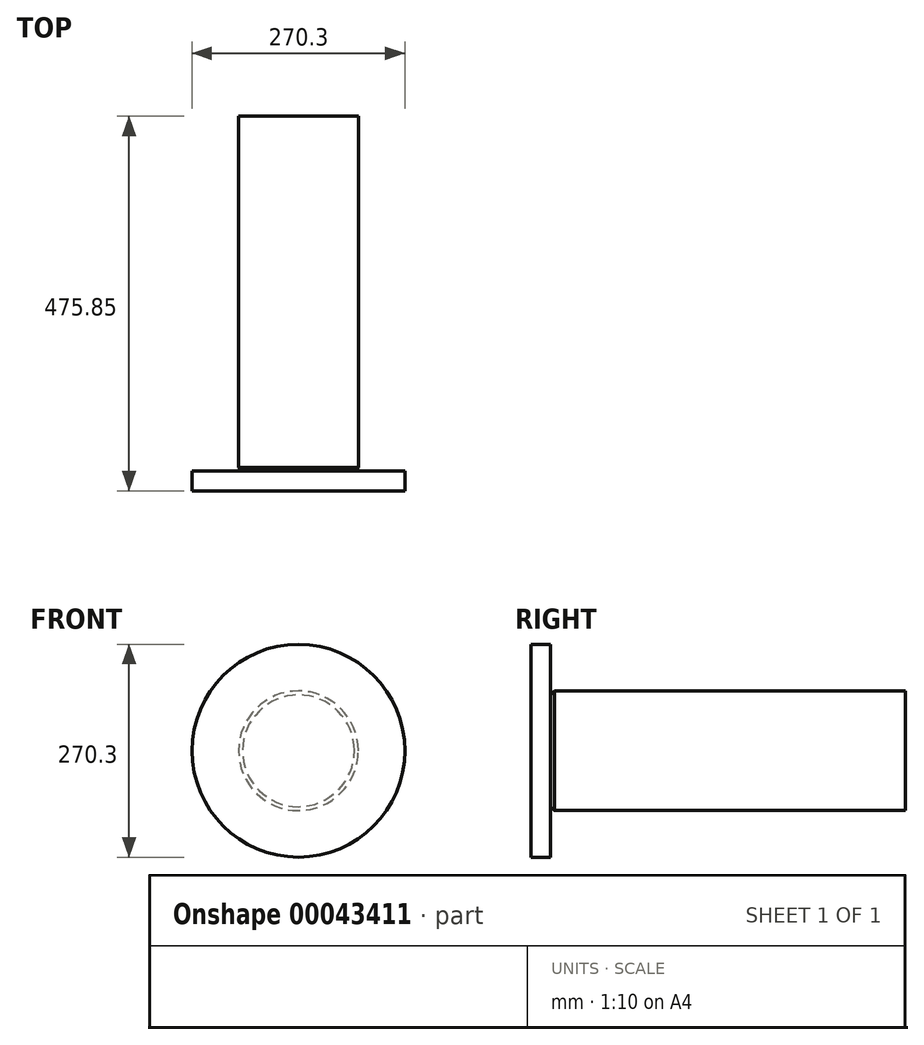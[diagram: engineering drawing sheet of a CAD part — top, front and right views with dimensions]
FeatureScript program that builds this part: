
annotation { "Feature Type Name" : "Feature", "Feature Type Description" : "" }
export const myFeature = defineFeature(function(context is Context, id is Id, definition is map)
    precondition{}
    {
        {
            var Q0;
            Q0=qCreatedBy(makeId("Front.planeOp"),FACE);
            var sketch = newSketch(context, id + "F0", { "sketchPlane" : qUnion([Q0])});
            skCircle(sketch, "E0", {"center": v(0, 0) * mm, "radius": 76 * mm});
            skSolve(sketch);
        }
        {
            var Q0;
            Q0=makeQuery(id+"F0.imprint","IMPRINT",FACE,{"disambiguationData":[TD([[makeQuery(id+"F0.imprint","IMPRINT",EDGE,{"derivedFrom":sQuery(id+"F0.wireOp",EDGE,"E0")}),1.0]])]});
            extrude(context, id + "F1", {"entities" : qUnion([Q0]), "oppositeDirection" : true, "depth" : 450.85 * mm});
        }
        {
            var Q0;
            Q0=makeQuery(id+"F1.opExtrude","CAP_EDGE",EDGE,{"disambiguationData":[OSD([sQuery(id+"F0.wireOp",EDGE,"E0")])],"isStart":true});
            chamfer(context, id + "F2", {"entities" : qUnion([Q0]), "width" : 5 * mm, "tangentPropagation" : true});
        }
        {
            var Q0;
            Q0=qCreatedBy(makeId("Front.planeOp"),FACE);
            var sketch = newSketch(context, id + "F3", { "sketchPlane" : qUnion([Q0])});
            skCircle(sketch, "E1", {"center": v(0, 0) * mm, "radius": 135.15 * mm});
            skSolve(sketch);
        }
        {
            var Q0;
            Q0=makeQuery(id+"F3.imprint","IMPRINT",FACE,{"disambiguationData":[TD([[makeQuery(id+"F3.imprint","IMPRINT",EDGE,{"derivedFrom":sQuery(id+"F3.wireOp",EDGE,"E1")}),1.0]])]});
            extrude(context, id + "F4", {"entities" : qUnion([Q0]), "operationType" : NewBodyOperationType.ADD, "depth" : 25 * mm});
        }
    });
